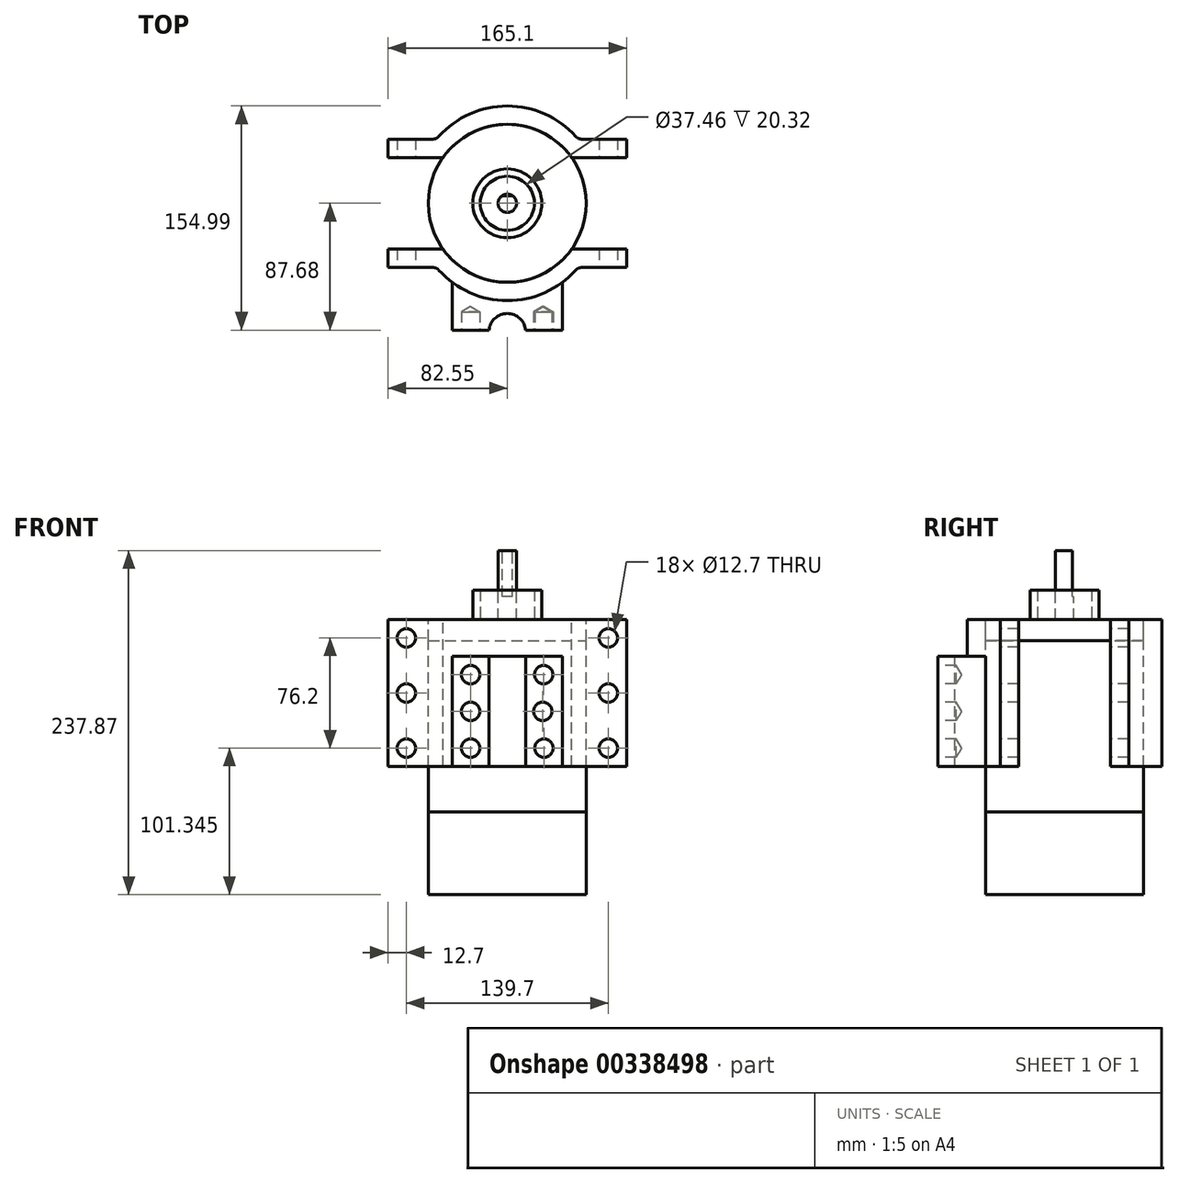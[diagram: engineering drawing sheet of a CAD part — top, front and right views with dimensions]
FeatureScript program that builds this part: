
annotation { "Feature Type Name" : "Feature", "Feature Type Description" : "" }
export const myFeature = defineFeature(function(context is Context, id is Id, definition is map)
    precondition{}
    {
        {
            var Q0;
            Q0=qCreatedBy(makeId("Top.planeOp"),FACE);
            var sketch = newSketch(context, id + "F0", { "sketchPlane" : qUnion([Q0])});
            skCircle(sketch, "E0", {"center": v(0, 0) * mm, "radius": 6.35 * mm});
            skSolve(sketch);
        }
        {
            var Q0;
            Q0=makeQuery(id+"F0.imprint","IMPRINT",FACE,{"disambiguationData":[TD([[makeQuery(id+"F0.imprint","IMPRINT",EDGE,{"derivedFrom":sQuery(id+"F0.wireOp",EDGE,"E0")}),1.0]])]});
            extrude(context, id + "F1", {"entities" : qUnion([Q0]), "oppositeDirection" : true, "depth" : 47.62 * mm});
        }
        {
            var Q0;
            Q0=makeQuery(id+"F1.opExtrude","CAP_FACE",FACE,{"disambiguationData":[OSD([sQuery(id+"F0.wireOp",EDGE,"E0")])],"isStart":true});
            var sketch = newSketch(context, id + "F2", { "sketchPlane" : qUnion([Q0])});
            skLineSegment(sketch, "E1", {"start": v(3.5, 5.3) * mm, "end": v(-3.5, 5.3) * mm});
            skSolve(sketch);
        }
        {
            var Q0;
            {var subQ0=sQuery(id+"F2.wireOp",EDGE,"E1");Q0=makeQuery(id+"F2.imprint","IMPRINT",FACE,{"disambiguationData":[TD([[makeQuery(id+"F2.imprint","IMPRINT",EDGE,{"derivedFrom":subQ0}),-1.0]])]});}
            extrude(context, id + "F3", {"entities" : qUnion([Q0]), "operationType" : NewBodyOperationType.REMOVE, "oppositeDirection" : true, "depth" : 31.75 * mm});
        }
        {
            var Q0;
            Q0=makeQuery(id+"F1.opExtrude","CAP_FACE",FACE,{"disambiguationData":[OSD([sQuery(id+"F0.wireOp",EDGE,"E0")])],"isStart":false});
            var sketch = newSketch(context, id + "F4", { "sketchPlane" : qUnion([Q0])});
            skCircle(sketch, "E2", {"center": v(0, 0) * mm, "radius": 18.73 * mm});
            skCircle(sketch, "E3", {"center": v(0, 0) * mm, "radius": 23.81 * mm});
            skSolve(sketch);
        }
        {
            var Q0;
            Q0=makeQuery(id+"F4.imprint","IMPRINT",FACE,{"disambiguationData":[TD([[makeQuery(id+"F4.imprint","IMPRINT",EDGE,{"derivedFrom":sQuery(id+"F4.wireOp",EDGE,"E2")}),-1.0]])]});
            extrude(context, id + "F5", {"entities" : qUnion([Q0]), "oppositeDirection" : true, "depth" : 20.32 * mm});
        }
        {
            var Q0;
            Q0=makeQuery(id+"F1.opExtrude","CAP_FACE",FACE,{"disambiguationData":[OSD([sQuery(id+"F0.wireOp",EDGE,"E0")])],"isStart":false});
            var sketch = newSketch(context, id + "F6", { "sketchPlane" : qUnion([Q0])});
            skCircle(sketch, "E4", {"center": v(0, 0) * mm, "radius": 54.61 * mm});
            skSolve(sketch);
        }
        {
            var Q0;
            Q0=makeQuery(id+"F6.imprint","IMPRINT",FACE,{"disambiguationData":[TD([[makeQuery(id+"F6.imprint","IMPRINT",EDGE,{"derivedFrom":sQuery(id+"F6.wireOp",EDGE,"E4")}),1.0]])]});
            var Q1;
            Q1=makeQuery(id+"F6.imprint","IMPRINT",FACE,{"disambiguationData":[TD([[makeQuery(id+"F6.imprint","IMPRINT",EDGE,{"derivedFrom":makeQuery(id+"F1.opExtrude","CAP_EDGE",EDGE,{"disambiguationData":[OSD([sQuery(id+"F0.wireOp",EDGE,"E0")])],"isStart":false})}),-1.0]])]});
            extrude(context, id + "F7", {"entities" : qUnion([Q0, Q1]), "depth" : 14.6 * mm});
        }
        {
            var Q0;
            Q0=makeQuery(id+"F7.opExtrude","CAP_FACE",FACE,{"disambiguationData":[OSD([sQuery(id+"F6.wireOp",EDGE,"E4")])],"isStart":false});
            var sketch = newSketch(context, id + "F8", { "sketchPlane" : qUnion([Q0])});
            skCircle(sketch, "E5", {"center": v(0, 0) * mm, "radius": 54.6 * mm});
            skSolve(sketch);
        }
        {
            var Q0;
            Q0=makeQuery(id+"F8.imprint","IMPRINT",FACE,{"disambiguationData":[TD([[makeQuery(id+"F8.imprint","IMPRINT",EDGE,{"derivedFrom":sQuery(id+"F8.wireOp",EDGE,"E5")}),1.0]])]});
            extrude(context, id + "F9", {"entities" : qUnion([Q0]), "operationType" : NewBodyOperationType.ADD, "depth" : 118.5 * mm});
        }
        {
            var Q0;
            Q0=makeQuery(id+"F9.opExtrude","CAP_FACE",FACE,{"disambiguationData":[OSD([sQuery(id+"F8.wireOp",EDGE,"E5")])],"isStart":false});
            var sketch = newSketch(context, id + "F10", { "sketchPlane" : qUnion([Q0])});
            skCircle(sketch, "E6", {"center": v(0, 0) * mm, "radius": 54.61 * mm});
            skSolve(sketch);
        }
        {
            var Q0;
            Q0=makeQuery(id+"F10.imprint","IMPRINT",FACE,{"disambiguationData":[TD([[makeQuery(id+"F10.imprint","IMPRINT",EDGE,{"derivedFrom":sQuery(id+"F10.wireOp",EDGE,"E6")}),1.0]])]});
            var Q1;
            Q1=makeQuery(id+"F10.imprint","IMPRINT",FACE,{"disambiguationData":[TD([[makeQuery(id+"F10.imprint","IMPRINT",EDGE,{"derivedFrom":makeQuery(id+"F9.opExtrude","CAP_EDGE",EDGE,{"disambiguationData":[OSD([sQuery(id+"F8.wireOp",EDGE,"E5")])],"isStart":false})}),1.0]])]});
            extrude(context, id + "F11", {"entities" : qUnion([Q0, Q1]), "operationType" : NewBodyOperationType.ADD, "depth" : 57.15 * mm});
        }
        {
            var Q0;
            Q0=makeQuery(id+"F7.opExtrude","CAP_FACE",FACE,{"disambiguationData":[OSD([sQuery(id+"F6.wireOp",EDGE,"E4")])],"isStart":true});
            var sketch = newSketch(context, id + "F12", { "sketchPlane" : qUnion([Q0])});
            skLineSegment(sketch, "E7", {"start": v(-44.45, 31.72) * mm, "end": v(44.45, 31.72) * mm});
            skPoint(sketch, "E8", {"position": v(0, 54.61) * mm});
            skArc(sketch, "E9", {"start": v(44.45, 31.72) * mm, "mid": v(0, 54.61) * mm, "end": v(-44.45, 31.72) * mm});
            skLineSegment(sketch, "E10", {"start": v(-44.45, 31.72) * mm, "end": v(-82.55, 31.72) * mm});
            skLineSegment(sketch, "E11", {"start": v(44.45, 31.72) * mm, "end": v(82.55, 31.72) * mm});
            skLineSegment(sketch, "E12", {"start": v(0, 54.61) * mm, "end": v(0, 67.31) * mm});
            skLineSegment(sketch, "E13", {"start": v(-82.55, 31.72) * mm, "end": v(-82.55, 44.42) * mm});
            skLineSegment(sketch, "E14", {"start": v(-82.55, 44.42) * mm, "end": v(-48.9, 44.42) * mm});
            skLineSegment(sketch, "E15", {"start": v(82.55, 31.72) * mm, "end": v(82.55, 44.42) * mm});
            skLineSegment(sketch, "E16", {"start": v(82.55, 44.42) * mm, "end": v(48.9, 44.42) * mm});
            skArc(sketch, "E17", {"start": v(48.9, 44.42) * mm, "mid": v(0, 67.31) * mm, "end": v(-48.9, 44.42) * mm});
            skSolve(sketch);
        }
        {
            var Q0;
            {var subQ0=sQuery(id+"F12.wireOp",EDGE,"E10");Q0=makeQuery(id+"F12.imprint","IMPRINT",FACE,{"disambiguationData":[TD([[makeQuery(id+"F12.imprint","IMPRINT",EDGE,{"derivedFrom":subQ0}),-1.0]])]});}
            var Q1;
            {var subQ0=sQuery(id+"F12.wireOp",EDGE,"E11");Q1=makeQuery(id+"F12.imprint","IMPRINT",FACE,{"disambiguationData":[TD([[makeQuery(id+"F12.imprint","IMPRINT",EDGE,{"derivedFrom":subQ0}),1.0]])]});}
            extrude(context, id + "F13", {"entities" : qUnion([Q0, Q1]), "oppositeDirection" : true, "depth" : 101.6 * mm});
        }
        {
            var Q0;
            Q0=makeQuery(id+"F7.opExtrude","CAP_FACE",FACE,{"disambiguationData":[OSD([sQuery(id+"F6.wireOp",EDGE,"E4")])],"isStart":true});
            var sketch = newSketch(context, id + "F14", { "sketchPlane" : qUnion([Q0])});
            skLineSegment(sketch, "E18", {"start": v(-44.45, -31.72) * mm, "end": v(44.45, -31.72) * mm});
            skPoint(sketch, "E19", {"position": v(0, -54.61) * mm});
            skArc(sketch, "E20", {"start": v(-44.45, -31.72) * mm, "mid": v(0, -54.61) * mm, "end": v(44.45, -31.72) * mm});
            skLineSegment(sketch, "E21", {"start": v(-44.45, -31.72) * mm, "end": v(-82.55, -31.72) * mm});
            skLineSegment(sketch, "E22", {"start": v(44.45, -31.72) * mm, "end": v(82.55, -31.72) * mm});
            skLineSegment(sketch, "E23", {"start": v(0, -54.61) * mm, "end": v(0, -67.31) * mm});
            skLineSegment(sketch, "E24", {"start": v(-82.55, -31.72) * mm, "end": v(-82.55, -44.42) * mm});
            skLineSegment(sketch, "E25", {"start": v(-82.55, -44.42) * mm, "end": v(-48.9, -44.42) * mm});
            skLineSegment(sketch, "E26", {"start": v(82.55, -31.72) * mm, "end": v(82.55, -44.42) * mm});
            skLineSegment(sketch, "E27", {"start": v(82.55, -44.42) * mm, "end": v(48.9, -44.42) * mm});
            skArc(sketch, "E28", {"start": v(-48.9, -44.42) * mm, "mid": v(0, -67.31) * mm, "end": v(48.9, -44.42) * mm});
            skSolve(sketch);
        }
        {
            var Q0;
            {var subQ0=sQuery(id+"F14.wireOp",EDGE,"E22");Q0=makeQuery(id+"F14.imprint","IMPRINT",FACE,{"disambiguationData":[TD([[makeQuery(id+"F14.imprint","IMPRINT",EDGE,{"derivedFrom":subQ0}),-1.0]])]});}
            var Q1;
            {var subQ0=sQuery(id+"F14.wireOp",EDGE,"E21");Q1=makeQuery(id+"F14.imprint","IMPRINT",FACE,{"disambiguationData":[TD([[makeQuery(id+"F14.imprint","IMPRINT",EDGE,{"derivedFrom":subQ0}),1.0]])]});}
            extrude(context, id + "F15", {"entities" : qUnion([Q0, Q1]), "oppositeDirection" : true, "depth" : 25.4 * mm});
        }
        {
            var Q0;
            {var subQ0=sQuery(id+"F14.wireOp",EDGE,"E25");var subQ2=sQuery(id+"F14.wireOp",EDGE,"E20");var subQ3=sQuery(id+"F14.wireOp",EDGE,"E21");var subQ4=sQuery(id+"F14.wireOp",EDGE,"E24");var subQ5=sQuery(id+"F14.wireOp",EDGE,"E28");Q0=makeQuery(id+"Fq8fBj3KPbGBi3Q_5.boolean.opBoolean","SPLIT",FACE,{"disambiguationData":[TD([makeQuery(id+"F15.opExtrude","SWEPT_FACE",FACE,{"disambiguationData":[OSD([subQ3])]})])],"derivedFrom":makeQuery(id+"F15.opExtrude","CAP_FACE",FACE,{"disambiguationData":[OSD([subQ2,subQ3,sQuery(id+"F14.wireOp",EDGE,"E22"),subQ4,subQ0,sQuery(id+"F14.wireOp",EDGE,"E26"),sQuery(id+"F14.wireOp",EDGE,"E27"),subQ5])],"isStart":false})});}
            var Q1;
            {var subQ0=sQuery(id+"F14.wireOp",EDGE,"E27");var subQ1=sQuery(id+"F14.wireOp",EDGE,"E26");var subQ2=sQuery(id+"F14.wireOp",EDGE,"E22");var subQ3=sQuery(id+"F14.wireOp",EDGE,"E20");var subQ4=sQuery(id+"F14.wireOp",EDGE,"E28");Q1=makeQuery(id+"Fq8fBj3KPbGBi3Q_5.boolean.opBoolean","SPLIT",FACE,{"disambiguationData":[TD([makeQuery(id+"F15.opExtrude","SWEPT_FACE",FACE,{"disambiguationData":[OSD([subQ2])]})])],"derivedFrom":makeQuery(id+"F15.opExtrude","CAP_FACE",FACE,{"disambiguationData":[OSD([subQ3,sQuery(id+"F14.wireOp",EDGE,"E21"),subQ2,sQuery(id+"F14.wireOp",EDGE,"E24"),sQuery(id+"F14.wireOp",EDGE,"E25"),subQ1,subQ0,subQ4])],"isStart":false})});}
            extrude(context, id + "F16", {"entities" : qUnion([Q0, Q1]), "operationType" : NewBodyOperationType.ADD, "depth" : 76.2 * mm});
        }
        {
            var Q0;
            Q0=makeQuery(id+"F16.opExtrude","CAP_FACE",FACE,{"disambiguationData":[OSD([sQuery(id+"F14.wireOp",EDGE,"E20"),sQuery(id+"F14.wireOp",EDGE,"E21"),sQuery(id+"F14.wireOp",EDGE,"E22"),sQuery(id+"F14.wireOp",EDGE,"E24"),sQuery(id+"F14.wireOp",EDGE,"E25"),sQuery(id+"F14.wireOp",EDGE,"E26"),sQuery(id+"F14.wireOp",EDGE,"E27"),sQuery(id+"F14.wireOp",EDGE,"E28")])],"isStart":false});
            var sketch = newSketch(context, id + "F17", { "sketchPlane" : qUnion([Q0])});
            skPoint(sketch, "E29", {"position": v(0, 67.31) * mm});
            skLineSegment(sketch, "E30", {"start": v(-38.1, 54.66) * mm, "end": v(-38.1, 87.68) * mm});
            skLineSegment(sketch, "E31", {"start": v(38.1, 54.66) * mm, "end": v(38.1, 87.68) * mm});
            skLineSegment(sketch, "E32", {"start": v(38.1, 87.68) * mm, "end": v(12.7, 87.68) * mm});
            skPoint(sketch, "E33", {"position": v(0, 76.2) * mm});
            skLineSegment(sketch, "E34", {"start": v(-38.1, 87.68) * mm, "end": v(-12.7, 87.68) * mm});
            skArc(sketch, "E35", {"start": v(-12.7, 87.68) * mm, "mid": v(0, 76.2) * mm, "end": v(12.7, 87.68) * mm});
            skSolve(sketch);
        }
        {
            var Q0;
            {var subQ0=sQuery(id+"F17.wireOp",EDGE,"E30");Q0=makeQuery(id+"F17.imprint","IMPRINT",FACE,{"disambiguationData":[TD([[makeQuery(id+"F17.imprint","IMPRINT",EDGE,{"derivedFrom":subQ0}),-1.0]])]});}
            extrude(context, id + "F18", {"entities" : qUnion([Q0]), "operationType" : NewBodyOperationType.ADD, "oppositeDirection" : true, "depth" : 76.2 * mm});
        }
        {
            var Q0;
            Q0=makeQuery(id+"F18.opExtrude","SWEPT_FACE",FACE,{"disambiguationData":[OSD([sQuery(id+"F17.wireOp",EDGE,"E34")])]});
            var sketch = newSketch(context, id + "F19", { "sketchPlane" : qUnion([Q0])});
            skCircle(sketch, "E36", {"center": v(-25.4, -85.72) * mm, "radius": 6.35 * mm});
            skCircle(sketch, "E37", {"center": v(-25.4, -111.12) * mm, "radius": 6.35 * mm});
            skCircle(sketch, "E38", {"center": v(-25.4, -136.53) * mm, "radius": 6.35 * mm});
            skCircle(sketch, "E39", {"center": v(25.17, -85.72) * mm, "radius": 6.35 * mm});
            skCircle(sketch, "E40", {"center": v(24.53, -111.12) * mm, "radius": 6.35 * mm});
            skCircle(sketch, "E41", {"center": v(25.35, -136.53) * mm, "radius": 6.35 * mm});
            skSolve(sketch);
        }
        {
            var Q0;
            Q0=sQuery(id+"F19.wireOp",VERTEX,"E36.center");
            var Q1;
            Q1=sQuery(id+"F19.wireOp",VERTEX,"E39.center");
            var Q2;
            Q2=sQuery(id+"F19.wireOp",VERTEX,"E37.center");
            var Q3;
            Q3=sQuery(id+"F19.wireOp",VERTEX,"E40.center");
            var Q4;
            Q4=sQuery(id+"F19.wireOp",VERTEX,"E38.center");
            var Q5;
            Q5=sQuery(id+"F19.wireOp",VERTEX,"E41.center");
            var Q6;
            Q6=makeQuery(id+"F15.opExtrude","SWEPT_BODY",BODY,{"disambiguationData":[OSD([sQuery(id+"F14.wireOp",EDGE,"E20"),sQuery(id+"F14.wireOp",EDGE,"E21"),sQuery(id+"F14.wireOp",EDGE,"E22"),sQuery(id+"F14.wireOp",EDGE,"E24"),sQuery(id+"F14.wireOp",EDGE,"E25"),sQuery(id+"F14.wireOp",EDGE,"E26"),sQuery(id+"F14.wireOp",EDGE,"E27"),sQuery(id+"F14.wireOp",EDGE,"E28")])]});
            hole(context, id + "F20", {"style" : HoleStyle.SIMPLE, "endStyle" : HoleEndStyle.BLIND, "holeDiameter" : 12.7 * mm, "holeDepth" : 12.7 * mm, "isTappedThrough" : true, "tappedDepth" : 12.7 * mm, "tapClearance" : 3, "startFromSketch" : true, "locations" : qUnion([Q0, Q1, Q2, Q3, Q4, Q5]), "scope" : qUnion([Q6])});
        }
        {
            var Q0;
            {var subQ0=sQuery(id+"F14.wireOp",EDGE,"E25");Q0=makeQuery(id+"F16.boolean.opBoolean","MERGE",FACE,{"derivedFrom":[makeQuery(id+"F15.opExtrude","SWEPT_FACE",FACE,{"disambiguationData":[OSD([subQ0])]}),makeQuery(id+"F16.opExtrude","SWEPT_FACE",FACE,{"disambiguationData":[OSD([subQ0])]})]});}
            var sketch = newSketch(context, id + "F21", { "sketchPlane" : qUnion([Q0])});
            skCircle(sketch, "E42", {"center": v(-69.85, -60.33) * mm, "radius": 6.35 * mm});
            skCircle(sketch, "E43", {"center": v(-69.85, -98.42) * mm, "radius": 6.35 * mm});
            skCircle(sketch, "E44", {"center": v(-69.85, -136.53) * mm, "radius": 6.35 * mm});
            skCircle(sketch, "E45", {"center": v(69.85, -60.33) * mm, "radius": 6.35 * mm});
            skCircle(sketch, "E46", {"center": v(69.85, -98.42) * mm, "radius": 6.35 * mm});
            skCircle(sketch, "E47", {"center": v(69.85, -136.53) * mm, "radius": 6.35 * mm});
            skSolve(sketch);
        }
        {
            var Q0;
            Q0=sQuery(id+"F21.wireOp",VERTEX,"E42.center");
            var Q1;
            Q1=sQuery(id+"F21.wireOp",VERTEX,"E43.center");
            var Q2;
            Q2=sQuery(id+"F21.wireOp",VERTEX,"E44.center");
            var Q3;
            Q3=sQuery(id+"F21.wireOp",VERTEX,"E45.center");
            var Q4;
            Q4=sQuery(id+"F21.wireOp",VERTEX,"E46.center");
            var Q5;
            Q5=sQuery(id+"F21.wireOp",VERTEX,"E47.center");
            var Q6;
            Q6=makeQuery(id+"F15.opExtrude","SWEPT_BODY",BODY,{"disambiguationData":[OSD([sQuery(id+"F14.wireOp",EDGE,"E20"),sQuery(id+"F14.wireOp",EDGE,"E21"),sQuery(id+"F14.wireOp",EDGE,"E22"),sQuery(id+"F14.wireOp",EDGE,"E24"),sQuery(id+"F14.wireOp",EDGE,"E25"),sQuery(id+"F14.wireOp",EDGE,"E26"),sQuery(id+"F14.wireOp",EDGE,"E27"),sQuery(id+"F14.wireOp",EDGE,"E28")])]});
            var Q7;
            Q7=makeQuery(id+"F13.opExtrude","SWEPT_BODY",BODY,{"disambiguationData":[OSD([sQuery(id+"F12.wireOp",EDGE,"E9"),sQuery(id+"F12.wireOp",EDGE,"E10"),sQuery(id+"F12.wireOp",EDGE,"E11"),sQuery(id+"F12.wireOp",EDGE,"E13"),sQuery(id+"F12.wireOp",EDGE,"E14"),sQuery(id+"F12.wireOp",EDGE,"E15"),sQuery(id+"F12.wireOp",EDGE,"E16"),sQuery(id+"F12.wireOp",EDGE,"E17")])]});
            hole(context, id + "F22", {"style" : HoleStyle.SIMPLE, "endStyle" : HoleEndStyle.THROUGH, "holeDiameter" : 12.7 * mm, "isTappedThrough" : true, "tappedDepth" : 12.7 * mm, "tapClearance" : 3, "startFromSketch" : true, "locations" : qUnion([Q0, Q1, Q2, Q3, Q4, Q5]), "scope" : qUnion([Q6, Q7])});
        }
        {
            var Q0;
            Q0=makeQuery(id+"F18.opExtrude","SWEPT_EDGE",EDGE,{"disambiguationData":[OSD([sQuery(id+"F14.wireOp",EDGE,"E28"),sQuery(id+"F17.wireOp",EDGE,"E30")])]});
            var Q1;
            Q1=makeQuery(id+"F18.opExtrude","CAP_EDGE",EDGE,{"disambiguationData":[OSD([sQuery(id+"F14.wireOp",EDGE,"E28")])],"isStart":false});
            var Q2;
            Q2=makeQuery(id+"F18.opExtrude","SWEPT_EDGE",EDGE,{"disambiguationData":[OSD([sQuery(id+"F14.wireOp",EDGE,"E28"),sQuery(id+"F17.wireOp",EDGE,"E31")])]});
            var Q3;
            {var subQ0=sQuery(id+"F14.wireOp",EDGE,"E28");var subQ1=sQuery(id+"F14.wireOp",EDGE,"E27");Q3=makeQuery(id+"F16.boolean.opBoolean","MERGE",EDGE,{"derivedFrom":[makeQuery(id+"F15.opExtrude","SWEPT_EDGE",EDGE,{"disambiguationData":[OSD([subQ1,subQ0])]}),makeQuery(id+"F16.opExtrude","SWEPT_EDGE",EDGE,{"disambiguationData":[OSD([subQ1,subQ0])]})]});}
            var Q4;
            {var subQ0=sQuery(id+"F14.wireOp",EDGE,"E28");var subQ1=sQuery(id+"F14.wireOp",EDGE,"E25");Q4=makeQuery(id+"F16.boolean.opBoolean","MERGE",EDGE,{"derivedFrom":[makeQuery(id+"F15.opExtrude","SWEPT_EDGE",EDGE,{"disambiguationData":[OSD([subQ1,subQ0])]}),makeQuery(id+"F16.opExtrude","SWEPT_EDGE",EDGE,{"disambiguationData":[OSD([subQ1,subQ0])]})]});}
            var Q5;
            Q5=makeQuery(id+"F13.opExtrude","SWEPT_EDGE",EDGE,{"disambiguationData":[OSD([sQuery(id+"F12.wireOp",EDGE,"E14"),sQuery(id+"F12.wireOp",EDGE,"E17")])]});
            var Q6;
            Q6=makeQuery(id+"F13.opExtrude","SWEPT_EDGE",EDGE,{"disambiguationData":[OSD([sQuery(id+"F12.wireOp",EDGE,"E16"),sQuery(id+"F12.wireOp",EDGE,"E17")])]});
            fillet(context, id + "F23", {"entities" : qUnion([Q0, Q1, Q2, Q3, Q4, Q5, Q6]), "radius" : 5.08 * mm, "tangentPropagation" : true, "allowEdgeOverflow" : false});
        }
    });
